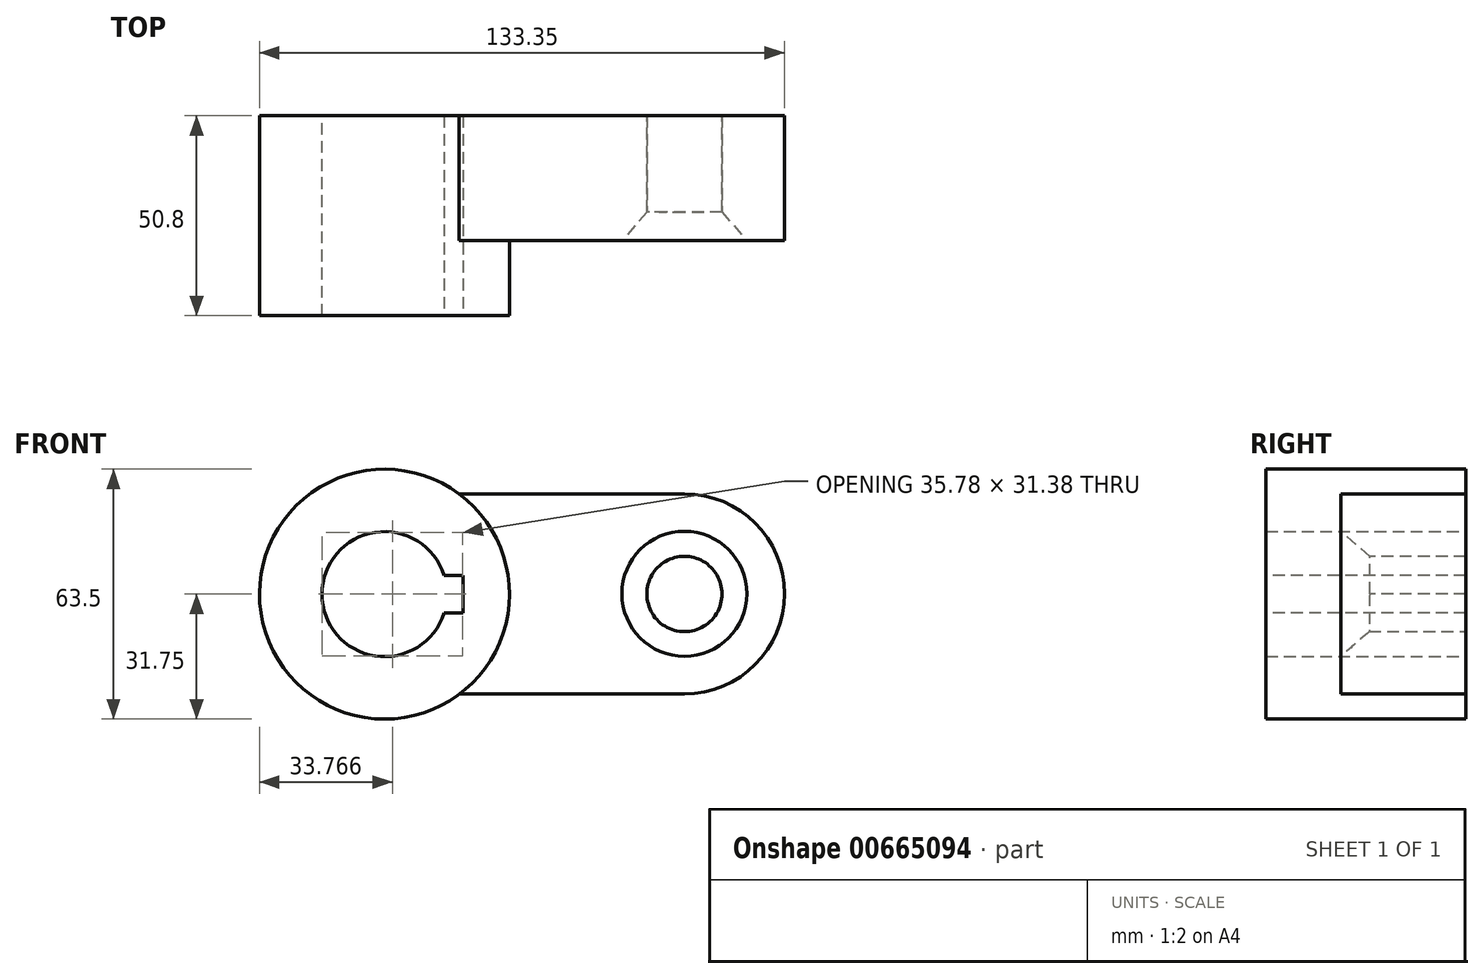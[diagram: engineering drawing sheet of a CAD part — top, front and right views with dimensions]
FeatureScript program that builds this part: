
annotation { "Feature Type Name" : "Feature", "Feature Type Description" : "" }
export const myFeature = defineFeature(function(context is Context, id is Id, definition is map)
    precondition{}
    {
        {
            var Q0;
            Q0=qCreatedBy(makeId("Front.planeOp"),FACE);
            var sketch = newSketch(context, id + "F0", { "sketchPlane" : qUnion([Q0])});
            skCircle(sketch, "E0", {"center": v(0, 0) * mm, "radius": 31.75 * mm});
            skCircle(sketch, "E1", {"center": v(0, 0) * mm, "radius": 15.88 * mm});
            skSolve(sketch);
        }
        {
            var Q0;
            Q0=makeQuery(id+"F0.imprint","IMPRINT",FACE,{"disambiguationData":[TD([[makeQuery(id+"F0.imprint","IMPRINT",EDGE,{"derivedFrom":sQuery(id+"F0.wireOp",EDGE,"E0")}),1.0]])]});
            extrude(context, id + "F1", {"entities" : qUnion([Q0]), "depth" : 50.8 * mm, "offsetDistance" : 25.4 * mm});
        }
        {
            var Q0;
            Q0=qCreatedBy(makeId("Front.planeOp"),FACE);
            var sketch = newSketch(context, id + "F2", { "sketchPlane" : qUnion([Q0])});
            skCircle(sketch, "E2", {"center": v(76.2, 0) * mm, "radius": 9.53 * mm});
            skLineSegment(sketch, "E3", {"start": v(18.48, 25.5) * mm, "end": v(18.48, -25.3) * mm});
            skLineSegment(sketch, "E4", {"start": v(18.48, -25.3) * mm, "end": v(76.2, -25.3) * mm});
            skLineSegment(sketch, "E5", {"start": v(18.48, 25.5) * mm, "end": v(76.2, 25.5) * mm});
            skArc(sketch, "E6", {"start": v(76.2, -25.3) * mm, "mid": v(101.6, 0.1) * mm, "end": v(76.2, 25.5) * mm});
            skSolve(sketch);
        }
        {
            var Q0;
            Q0=makeQuery(id+"F2.imprint","IMPRINT",FACE,{"disambiguationData":[TD([[makeQuery(id+"F2.imprint","IMPRINT",EDGE,{"derivedFrom":sQuery(id+"F2.wireOp",EDGE,"E2")}),-1.0]])]});
            extrude(context, id + "F3", {"entities" : qUnion([Q0]), "operationType" : NewBodyOperationType.ADD, "depth" : 31.75 * mm, "offsetDistance" : 25.4 * mm});
        }
        {
            var Q0;
            Q0=makeQuery(id+"F3.opExtrude","CAP_FACE",FACE,{"disambiguationData":[OSD([sQuery(id+"F2.wireOp",EDGE,"E2"),sQuery(id+"F2.wireOp",EDGE,"E3"),sQuery(id+"F2.wireOp",EDGE,"E4"),sQuery(id+"F2.wireOp",EDGE,"E5"),sQuery(id+"F2.wireOp",EDGE,"E6")])],"isStart":false});
            var sketch = newSketch(context, id + "F4", { "sketchPlane" : qUnion([Q0])});
            skCircle(sketch, "E7", {"center": v(76.2, 0.1) * mm, "radius": 15.88 * mm});
            skSolve(sketch);
        }
        {
            var Q0;
            Q0=sQuery(id+"F4.wireOp",VERTEX,"E7.center");
            var Q1;
            Q1=makeQuery(id+"F1.opExtrude","SWEPT_BODY",BODY,{"disambiguationData":[OSD([sQuery(id+"F0.wireOp",EDGE,"E0"),sQuery(id+"F0.wireOp",EDGE,"E1")])]});
            hole(context, id + "F5", {"style" : HoleStyle.C_SINK, "endStyle" : HoleEndStyle.THROUGH, "holeDiameter" : 19.05 * mm, "cSinkDiameter" : 31.75 * mm, "cSinkAngle" : 82 * degree, "majorDiameter" : 6.35 * mm, "isTappedThrough" : true, "tappedDepth" : 12.7 * mm, "tapClearance" : 3, "locations" : qUnion([Q0]), "scope" : qUnion([Q1])});
        }
        {
            var Q0;
            Q0=makeQuery(id+"F1.opExtrude","CAP_FACE",FACE,{"disambiguationData":[OSD([sQuery(id+"F0.wireOp",EDGE,"E0"),sQuery(id+"F0.wireOp",EDGE,"E1")])],"isStart":false});
            var sketch = newSketch(context, id + "F6", { "sketchPlane" : qUnion([Q0])});
            skLineSegment(sketch, "E8", {"start": v(15.14, -4.76) * mm, "end": v(15.14, 4.76) * mm});
            skLineSegment(sketch, "E9", {"start": v(15.14, 4.76) * mm, "end": v(19.9, 4.76) * mm});
            skLineSegment(sketch, "E10", {"start": v(19.9, 4.76) * mm, "end": v(19.9, -4.76) * mm});
            skLineSegment(sketch, "E11", {"start": v(19.9, -4.76) * mm, "end": v(15.14, -4.76) * mm});
            skSolve(sketch);
        }
        {
            var Q0;
            {var subQ0=sQuery(id+"F6.wireOp",EDGE,"E9");Q0=makeQuery(id+"F6.imprint","IMPRINT",FACE,{"disambiguationData":[TD([[makeQuery(id+"F6.imprint","IMPRINT",EDGE,{"derivedFrom":subQ0}),-1.0]])]});}
            extrude(context, id + "F7", {"entities" : qUnion([Q0]), "operationType" : NewBodyOperationType.REMOVE, "oppositeDirection" : true, "depth" : 76.2 * mm, "offsetDistance" : 25.4 * mm});
        }
    });
